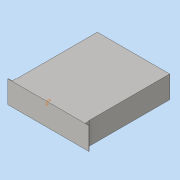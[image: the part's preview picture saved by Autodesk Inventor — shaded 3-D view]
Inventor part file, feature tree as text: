
AUTODESK INVENTOR PART (.ipt)
format: ipt  version: 2016 (Build 200138000, 138)  size: 101,888 bytes
history: native  units: in
note: dims shown in document units (in); Inventor stores cm internally (conversion verified against a paired STEP export)
features: extrude x2, sketch x2, plane x1, mirror x1
ambient origin geometry x8: Origin, YZ Plane, XZ Plane, XY Plane, X Axis, Y Axis, Z Axis, Center Point
bodies: Body1 (feature_tree)
feature tree (6):
  extrude  "Extrusion3"  Depth=20.0in
  plane  "Work Plane3"
  extrude  "Extrusion5"  Depth=1.0in
  mirror  "Mirror1"
  sketch  "Sketch2"  dims[d6=17.0in d7=20.0in]
  sketch  "Sketch4"  dims[d8=5.25in d9=0.0in d13=1.0in d14=1.0in d15=0.104in d16=5.25in d17=0.0in]
